# Revit family: Toilet-Floor_Mount-KOHLER-Veil-K-5401
name_source: partatom
category: Plumbing Fixtures
revit_build: Autodesk Revit 2017 (Build: 20160225_1515(x64)
units: mm (PartAtom-declared; Revit-internal decimal feet)

## family parameters
Cut with Voids When Loaded = No
Host = Face
OmniClass Number = 23.45.05.21.11
Part Type = Normal
Room Calculation Point = No
Round Connector Dimension = Use Diameter
Shared = No

## types (2) — shared parameters
Apparent Load = 1800 VA
Assembly Code = D2010100
CW Connection = Yes
Date Modified = 09/03/2019
Default Elevation = 0"
Description = Veil Intelligent skirted one-piece elongated dual-flush toilet
Electrical Connection = Yes
Electrical Note = One dedicated circuit required, protected with Class A Ground-Fault Circuit-Interrupter (GFCI) or Residual Current Device (RCD)
Finish = Kohler-Vitreous_China-0-White
Height = 21"
Inlet Connector = Inlet Connection
Length = 26 1/8"
Manufacturer = KOHLER Co.
MasterFormat 1995 = 15410
MasterFormat 2004 = 22.41.13
Material = Vitreous China
Outlet Connector = Outlet Connection
Pressure = 0.00 psi
Product Name = Veil
Product Page URL = http://www.us.kohler.com
Rough-In = 12"
URL = http://www.us.kohler.com
Voltage = 120 V
Waste Connection = Yes
WaterSense Certified = Yes
Width = 17 1/4"

## per-type parameters (varying)
| type | ADA Compliant | Flow Rate | Flush Rate- GPF | Flush Rate- LPF | Model | Product Documentation Link | Type |
| Unassisted, 0-White | No | 9 GPM | 1.28 gpf | 4.8 lpf | K-5401-0 | http://www.us.kohler.com | 0 |
| Pump Assisted, 0-White | Yes | 6 GPM | 1.19 gpf | 4.5 gpf | K-5401-PA-0 | https://www.us.kohler.com | 1 |

## geometry (parser evidence)
native form markers: Sweep x6
no freeform markers — native parametric forms only
